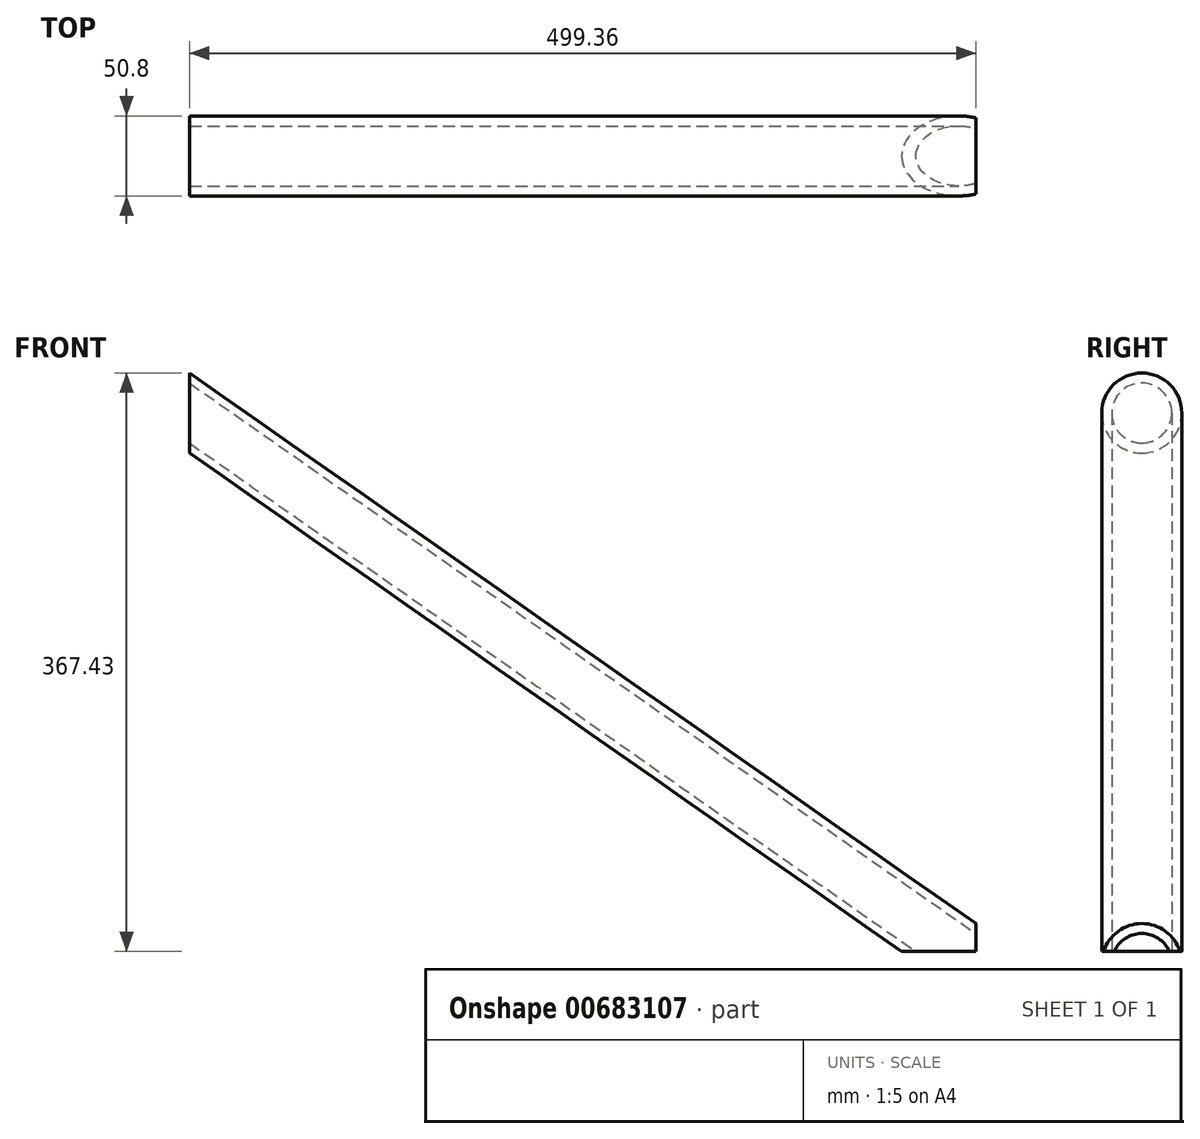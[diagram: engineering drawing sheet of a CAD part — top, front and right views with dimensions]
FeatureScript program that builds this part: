
annotation { "Feature Type Name" : "Feature", "Feature Type Description" : "" }
export const myFeature = defineFeature(function(context is Context, id is Id, definition is map)
    precondition{}
    {
        {
            var Q0;
            Q0=qCreatedBy(makeId("Right.planeOp"),FACE);
            var sketch = newSketch(context, id + "F0", { "sketchPlane" : qUnion([Q0])});
            skCircle(sketch, "E0", {"center": v(0, 0) * mm, "radius": 25.4 * mm});
            skCircle(sketch, "E1", {"center": v(0, 0) * mm, "radius": 19.05 * mm});
            skSolve(sketch);
        }
        {
            var Q0;
            Q0=qCreatedBy(makeId("Front.planeOp"),FACE);
            var sketch = newSketch(context, id + "F1", { "sketchPlane" : qUnion([Q0])});
            skLineSegment(sketch, "E2", {"start": v(0, 0) * mm, "end": v(-499.36, 349.65) * mm});
            skSolve(sketch);
        }
        {
            var Q0;
            Q0=makeQuery(id+"F0.imprint","IMPRINT",FACE,{"disambiguationData":[TD([[makeQuery(id+"F0.imprint","IMPRINT",EDGE,{"derivedFrom":sQuery(id+"F0.wireOp",EDGE,"E0")}),1.0]])]});
            var Q1;
            Q1=sQuery(id+"F1.wireOp",EDGE,"E2");
            sweep(context, id + "F2", {"profiles" : qUnion([Q0]), "path" : qUnion([Q1])});
        }
        {
            var Q0;
            Q0=makeQuery(id+"F2.opSweep","CAP_FACE",FACE,{"disambiguationData":[OSD([sQuery(id+"F0.wireOp",EDGE,"E0"),sQuery(id+"F1.wireOp",VERTEX,"E2.start")])],"isStart":true});
            var sketch = newSketch(context, id + "F3", { "sketchPlane" : qUnion([Q0])});
            skLineSegment(sketch, "E3.bottom", {"start": v(-25.4, 7.62) * mm, "end": v(25.4, 7.62) * mm});
            skLineSegment(sketch, "E3.top", {"start": v(-25.4, -25.4) * mm, "end": v(25.4, -25.4) * mm});
            skLineSegment(sketch, "E3.left", {"start": v(-25.4, 7.62) * mm, "end": v(-25.4, -25.4) * mm});
            skLineSegment(sketch, "E3.right", {"start": v(25.4, 7.62) * mm, "end": v(25.4, -25.4) * mm});
            skSolve(sketch);
        }
        {
            var Q0;
            Q0 = qSketchRegion(id + "F3", true);
            extrude(context, id + "F4", {"entities" : qUnion([Q0]), "operationType" : NewBodyOperationType.REMOVE, "endBound" : BoundingType.THROUGH_ALL, "oppositeDirection" : true, "depth" : 25.4 * mm, "offsetDistance" : 25.4 * mm});
        }
    });
